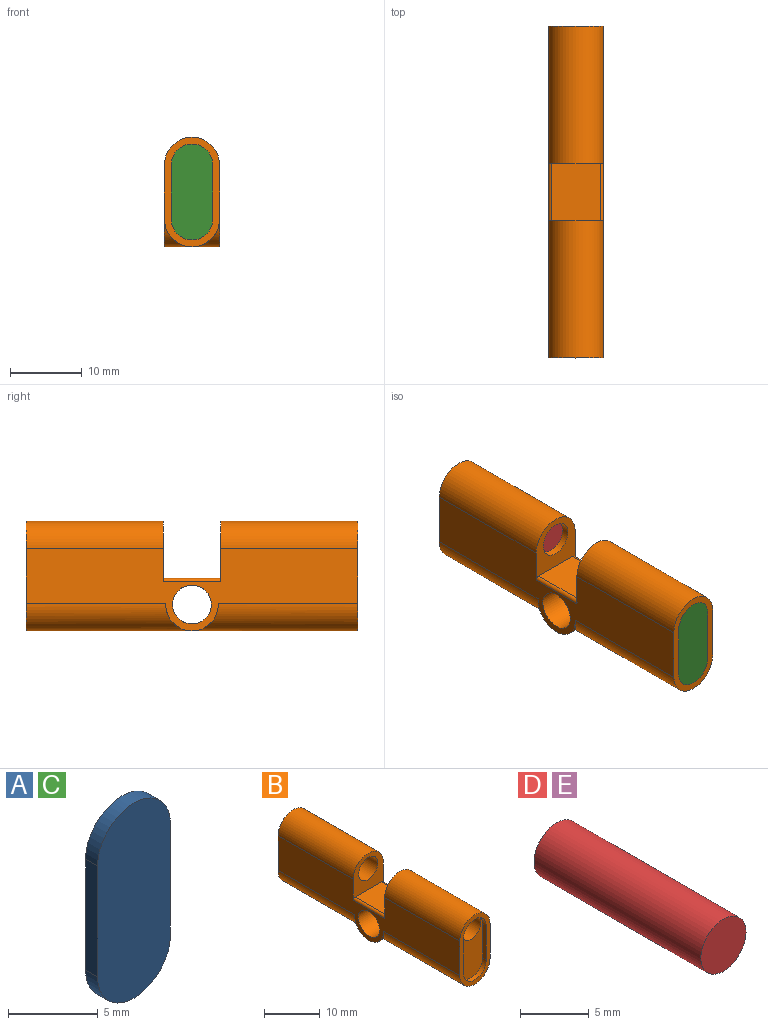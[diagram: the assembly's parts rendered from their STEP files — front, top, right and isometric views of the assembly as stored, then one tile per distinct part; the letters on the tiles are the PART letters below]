
ASSEMBLY  parts=5 mates=5
PART A: 6 faces, bbox 5.8x1x13.4 mm
  f0: plane 13.35x5.75mm, normal (0,1,0), area 69.7mm2, adj f1,f2,f3,f4
  f1: plane 7.6x0.95mm, normal (1,0,0), area 7.2mm2, adj f0,f2,f4,f5
  f2: cylinder r=2.88mm len=5.75mm, axis (0,-1,0), area 8.6mm2, adj f0,f1,f3,f5
  f3: plane 7.6x0.95mm, normal (-1,0,0), area 7.2mm2, adj f0,f2,f4,f5
  f4: cylinder r=2.88mm len=5.75mm, axis (0,-1,0), area 8.6mm2, adj f0,f1,f3,f5
  f5: plane 13.35x5.75mm, normal (0,-1,0), area 69.7mm2, adj f1,f2,f3,f4
PART B: 28 faces, bbox 7.7x46.2x15.3 mm
  f0: cylinder r=2.43mm len=18.13mm, axis (0,-1,0), area 276.2mm2, adj f7,f21
  f1: plane 15.25x7.65mm, normal (0,1,0), area 34.4mm2, adj f4,f5,f12,f13,f22,f23,f24,f25
  f2: cylinder r=2.43mm len=18.13mm, axis (0,-1,0), area 276.2mm2, adj f8,f16
  f3: cylinder r=3.82mm len=23.08mm, axis (0,-1,0), area 249mm2, adj f4,f5,f6,f14,f15
  f4: plane 46.15x11.43mm, normal (-1,0,0), area 313.2mm2, adj f1,f3,f6,f7,f8,f10,f11,f12
  f5: plane 46.15x11.43mm, normal (1,0,0), area 313.2mm2, adj f1,f3,f6,f7,f8,f10,f11,f12
  f6: plane 15.25x7.65mm, normal (0,-1,0), area 34.4mm2, adj f3,f4,f5,f11,f17,f18,f19,f20
  f7: plane 8.43x7.65mm, normal (0,-1,0), area 36.2mm2, adj f0,f4,f5,f9,f12,f26,f27
  f8: plane 8.43x7.65mm, normal (0,1,0), area 36.2mm2, adj f2,f4,f5,f9,f11,f26,f27
  f9: plane 8x6.7mm, normal (0,0,1), area 53.6mm2, adj f7,f8,f26,f27
  f10: cylinder r=2.7mm len=7.65mm, axis (1,0,0), area 129.8mm2, adj f4,f5
  f11: cylinder r=3.82mm len=19.08mm, axis (0,-1,0), area 229.2mm2, adj f4,f5,f6,f8
  f12: cylinder r=3.82mm len=19.08mm, axis (0,-1,0), area 229.2mm2, adj f1,f4,f5,f7
  f13: cylinder r=3.82mm len=23.08mm, axis (0,-1,0), area 249mm2, adj f1,f4,f5,f14,f15
  f14: cylinder r=3.65mm len=7.3mm, axis (1,0,0), area 16.3mm2, adj f3,f4,f13
  f15: cylinder r=3.65mm len=7.3mm, axis (1,0,0), area 16.3mm2, adj f3,f5,f13
  f16: plane 13.35x5.75mm, normal (0,-1,0), area 51.2mm2, adj f2,f17,f18,f19,f20
  f17: cylinder r=2.88mm len=5.75mm, axis (0,-1,0), area 8.6mm2, adj f6,f16,f18,f19
  f18: plane 7.6x0.95mm, normal (-1,0,0), area 7.2mm2, adj f6,f16,f17,f20
  f19: plane 7.6x0.95mm, normal (1,0,0), area 7.2mm2, adj f6,f16,f17,f20
  f20: cylinder r=2.88mm len=5.75mm, axis (0,-1,0), area 8.6mm2, adj f6,f16,f18,f19
  f21: plane 13.35x5.75mm, normal (0,1,0), area 51.2mm2, adj f0,f22,f23,f24,f25
  f22: cylinder r=2.88mm len=5.75mm, axis (0,1,0), area 8.6mm2, adj f1,f21,f23,f25
  f23: plane 7.6x0.95mm, normal (-1,0,0), area 7.2mm2, adj f1,f21,f22,f24
  f24: cylinder r=2.88mm len=5.75mm, axis (0,1,0), area 8.6mm2, adj f1,f21,f23,f25
  f25: plane 7.6x0.95mm, normal (1,0,0), area 7.2mm2, adj f1,f21,f22,f24
  f26: cylinder r=0.47mm len=8mm, axis (0,1,0), area 6mm2, adj f4,f7,f8,f9
  f27: cylinder r=0.47mm len=8mm, axis (0,1,0), area 6mm2, adj f5,f7,f8,f9
PART C: same geometry as A
PART D: 3 faces, bbox 4.7x17.2x4.7 mm
  f0: cylinder r=2.32mm len=17.18mm, axis (0,-1,0), area 250.9mm2, adj f1,f2
  f1: plane 4.65x4.65mm, normal (0,1,0), area 17mm2, adj f0
  f2: plane 4.65x4.65mm, normal (0,-1,0), area 17mm2, adj f0
PART E: same geometry as D
PLACE A t=(-20.31,58.65,-2.58)mm
PLACE B t=(-20.31,13.45,-2.58)mm fixed
PLACE C rot(axis=(1,0,0),180deg) t=(-20.31,-31.75,-2.58)mm
PLACE D t=(-20.31,40.52,-2.58)mm
PLACE E t=(-20.31,13.45,-2.58)mm
MATE fastened A.f0 <-> B.f1  axis (0,1,0) through (-20.31,36.52,-2.58)mm
MATE slider D.f0 <-> B.f0  axis (0,1,0) through (-20.31,35.57,1.67)mm
MATE slider B.f0 <-> E.f0  axis (0,-1,0) through (-20.31,-8.68,1.67)mm
MATE fastened C.f0 <-> B.f6  axis (0,-1,0) through (-20.31,-9.63,-2.58)mm
MATE parallel E.f0 <-> D.f0  axis (0,1,0) through (-20.31,8.5,1.67)mm
